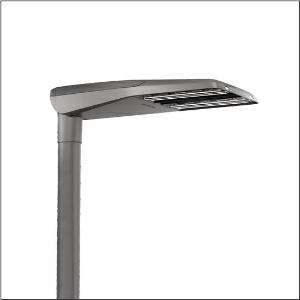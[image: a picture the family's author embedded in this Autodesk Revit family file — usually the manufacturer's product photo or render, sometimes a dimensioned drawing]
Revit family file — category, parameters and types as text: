
# Revit family: streetlight_sl_11_iq_midi___st1_0a_5xc3m41f08me_932e
name_source: partatom
category: Lighting Fixtures
units: mm (PartAtom-declared; Revit-internal decimal feet)

## family parameters
Cut with Voids When Loaded = No
Host = Face
Light Source = No
Part Type = Normal
Room Calculation Point = No
Round Connector Dimension = Use Diameter
Shared = No

## types (1)
- --- (1 x LED, 18310 lm, 124.7 W, 4000K)
    Apparent Load = 125 VA
    CIE Flux Codes = 33 66 96 100 100
    Color Rendering = 70
    Color Temperature = 4000K
    Default Elevation = 1800 mm
    Description = Streetlight SL 11 iQ midi, mast luminaire, primary light control with 3 zone facetted reflector, of plastic, silver coated, highly specular, primary optical cover: cover, of PMMA, transparent, light distribution: ST1.0a, light emission: direct distribution, primary light characteristic: asymmetric, installation type: post-top, side-entry, LED, High Power LED, rated luminous flux: 18.310lm, luminous efficacy: 147lm/W, light colour: 740, colour temperature: 4000K, control: optimised constant luminous flux control (CLO 2.0), Street-Remote, Desk-Remote (wireless, voltage-free reading and setting of iQ features in the workshop via application-optimized NFC function/RFID function), Light-Fading, Smart-Wire, Night-Set, Lumen-Switch, Temp-Guard, Auto-Match, with cable H07RN-F 5x 1.5mm², mains connection: 230..240V, AC, 50/60Hz, connection cable pre-assembled, cable length: 12,5m, start of lifetime: 125W, end of service life: 132W, reduction: 57W, luminaire housing, of diecast aluminium, powder-coated, Siteco® metallic grey (DB 702S), please order mast flange separately, inclination adjustable without tools: 0°, 5°, 10°, 15° (post-top) | 0°, -5°, -10°, -15° (side-entry), sealing non-destructively replaceable, multi-level sealing system, length: 780mm, width: 376mm, height: 118mm, mast flange for spigot size: 42mm (side-entry): 5XC10008XM4, 60/48mm (side-entry/post-top): 5XC10108XM2, 76/60mm (side-entry/post-top): 5XC10108XM1, equipment: Power, protection rating (complete): IP66, insulation class (complete): insulation class II (safety insulation), certification: CE, ENEC, VDE, impact resistance: IK09, permissible operating ambient temperature for outdoor applications: -25..+50°C, standard-compliant lighting for roads and squares, Environmental Product Declaration (EPD) tested and certified by an independent institute, packaging unit: 1 piece

Light Distribution: ST1.0a
    Height = 118 mm
    Lamp = 1 x LED
    Lamp Light Flux = 18310 lm
    Lamp Power = 124.7 W
    Lamp count = 1
    Length = 780 mm
    Luminous efficacy = 147 lm/W
    Manufacturer = Siteco
    ModVariant = No
    Model = 5XC3M41F08ME
    Number of Poles = 1
    OnlyDefault = Yes
    Power Factor = 1
    Product Name = Streetlight SL 11 iQ midi | ST1.0a
    Product group = mast luminaire | pylon top
    ProductGroupID = 6100
    Protection Class = Protection class II
    Protection Degree = IP 66
    RLX_Detail_Level = 1
    RLX_Emergency_Light_Flux = 0 lm
    RLX_Emergency_Type = 0
    RLX_Emergency_Type_DB = No
    RlxData = <blob elided: 70177 chars, md5=01a5b31b>
    Socket = socket
    Standby Power = 0 W
    System Light Flux = 18310 lm
    System Power = 125 W
    Type Comments = factory setting: luminous flux: 100 % | dim-lin: 254 | 557 mA
    Type Image = l_1005960.jpg
    URL = http://relux.com
    VarID = @adj_020853
    Voltage = 0 V
    Weight = 0.00 kg
    Width = 376 mm

## geometry (parser evidence)
native form markers: Blend x4, Sweep x10
no freeform markers — native parametric forms only
